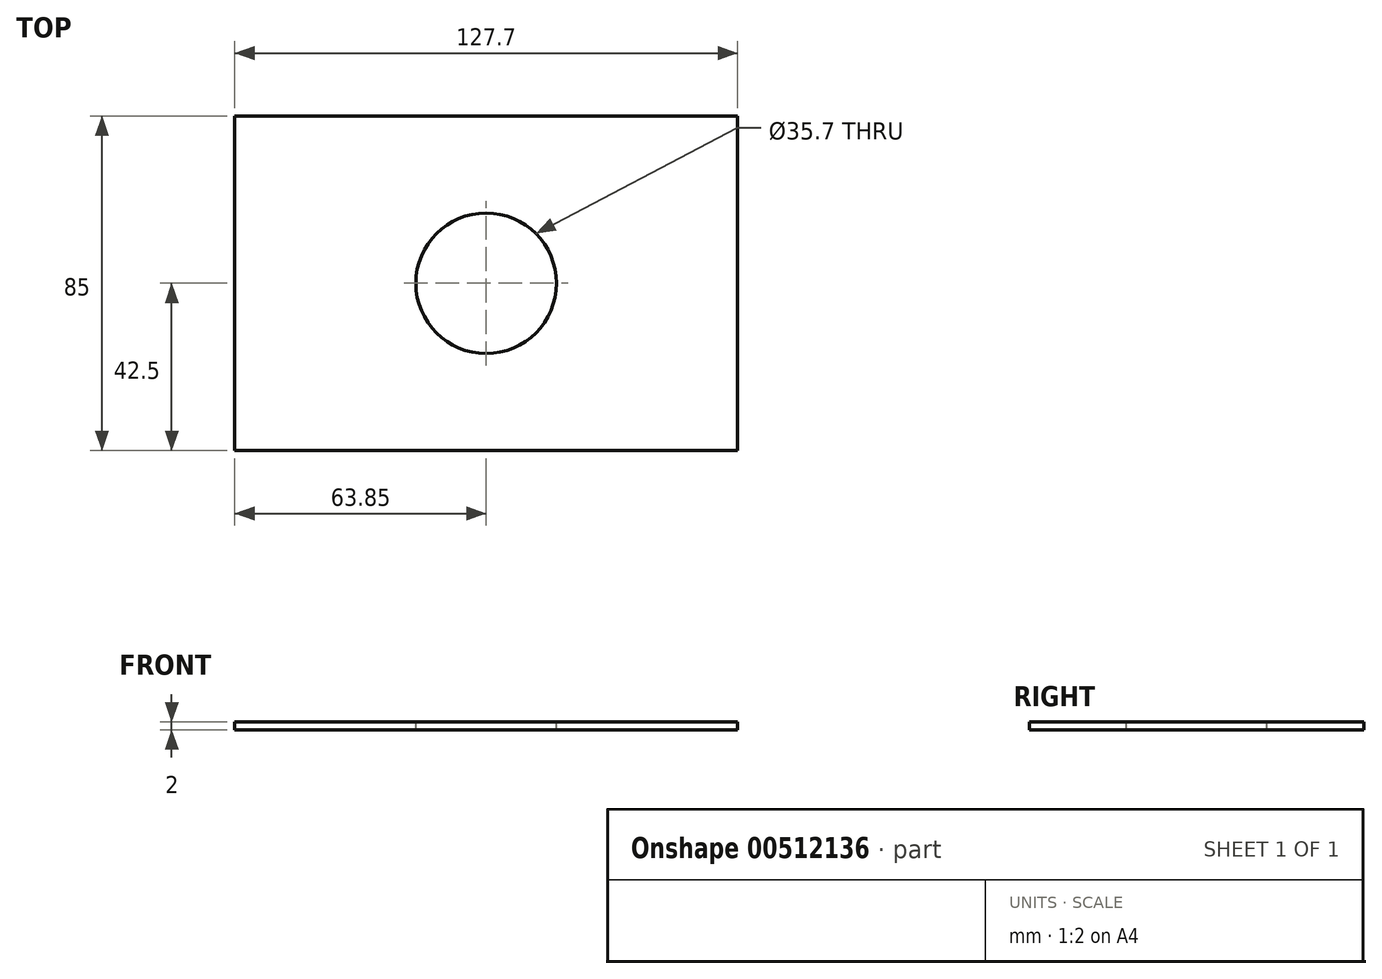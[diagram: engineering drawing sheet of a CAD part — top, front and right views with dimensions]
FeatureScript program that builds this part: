
annotation { "Feature Type Name" : "Feature", "Feature Type Description" : "" }
export const myFeature = defineFeature(function(context is Context, id is Id, definition is map)
    precondition{}
    {
        {
            assignVariable(context, id + "F0", {"name" : "s", "anyValue" : 2 * mm});
        }
        {
            var Q0;
            Q0=qCreatedBy(makeId("Top.planeOp"),FACE);
            cPlane(context, id + "F1", {"entities" : qUnion([Q0]), "cplaneType" : CPlaneType.OFFSET, "offset" : getVariable(context, 's'), "width" : 150 * mm, "height" : 150 * mm});
        }
        {
            var Q0;
            Q0=qCreatedBy(id+"F1.planeOp",FACE);
            var sketch = newSketch(context, id + "F2", { "sketchPlane" : qUnion([Q0])});
            skPoint(sketch, "E0.middle", {"position": v(0, 0) * mm});
            skLineSegment(sketch, "E1.bottom", {"start": v(-63.85, 42.5) * mm, "end": v(63.85, 42.5) * mm});
            skLineSegment(sketch, "E1.top", {"start": v(-63.85, -42.5) * mm, "end": v(63.85, -42.5) * mm});
            skLineSegment(sketch, "E1.left", {"start": v(-63.85, 42.5) * mm, "end": v(-63.85, -42.5) * mm});
            skLineSegment(sketch, "E1.right", {"start": v(63.85, 42.5) * mm, "end": v(63.85, -42.5) * mm});
            skLineSegment(sketch, "E2", {"start": v(-63.85, 42.5) * mm, "end": v(63.85, -42.5) * mm, "construction": true});
            skLineSegment(sketch, "E3", {"start": v(-63.85, -42.5) * mm, "end": v(63.85, 42.5) * mm, "construction": true});
            skCircle(sketch, "E4", {"center": v(0, 0) * mm, "radius": 17.85 * mm});
            skSolve(sketch);
        }
        {
            var Q0;
            Q0=makeQuery(id+"F2.imprint","IMPRINT",FACE,{"disambiguationData":[TD([[makeQuery(id+"F2.imprint","IMPRINT",EDGE,{"derivedFrom":sQuery(id+"F2.wireOp",EDGE,"E0.bottom")}),1.0]])]});
            var Q1;
            Q1=makeQuery(id+"F2.imprint","IMPRINT",FACE,{"disambiguationData":[TD([[makeQuery(id+"F2.imprint","IMPRINT",EDGE,{"derivedFrom":sQuery(id+"F2.wireOp",EDGE,"E1.bottom")}),-1.0]])]});
            var Q2;
            Q2=makeQuery(id+"F2.imprint","IMPRINT",FACE,{"disambiguationData":[TD([[makeQuery(id+"F2.imprint","IMPRINT",EDGE,{"derivedFrom":sQuery(id+"F2.wireOp",EDGE,"2ghOPRkr-yXzI-N56r-iC3q-vcRzsDxk2fJS.bottom")}),1.0]])]});
            var Q3;
            Q3=makeQuery(id+"F2.imprint","IMPRINT",FACE,{"disambiguationData":[TD([[makeQuery(id+"F2.imprint","IMPRINT",EDGE,{"derivedFrom":sQuery(id+"F2.wireOp",EDGE,"f8459f5c-8e0b-46e5-9303-0bab73200581.right")}),-1.0]])]});
            var Q4;
            {var subQ3=sQuery(id+"F2.wireOp",EDGE,"b7aDm1R6-ZlvE-9BxU-Uveq-xgOsrHnOjqtT");Q4=makeQuery(id+"F2.imprint","IMPRINT",FACE,{"disambiguationData":[TD([[makeQuery(id+"F2.imprint","IMPRINT",EDGE,{"derivedFrom":subQ3}),-1.0]])]});}
            extrude(context, id + "F3", {"entities" : qUnion([Q0, Q1, Q2, Q3, Q4]), "oppositeDirection" : true, "depth" : getVariable(context, 's'), "offsetDistance" : 25 * mm});
        }
    });
